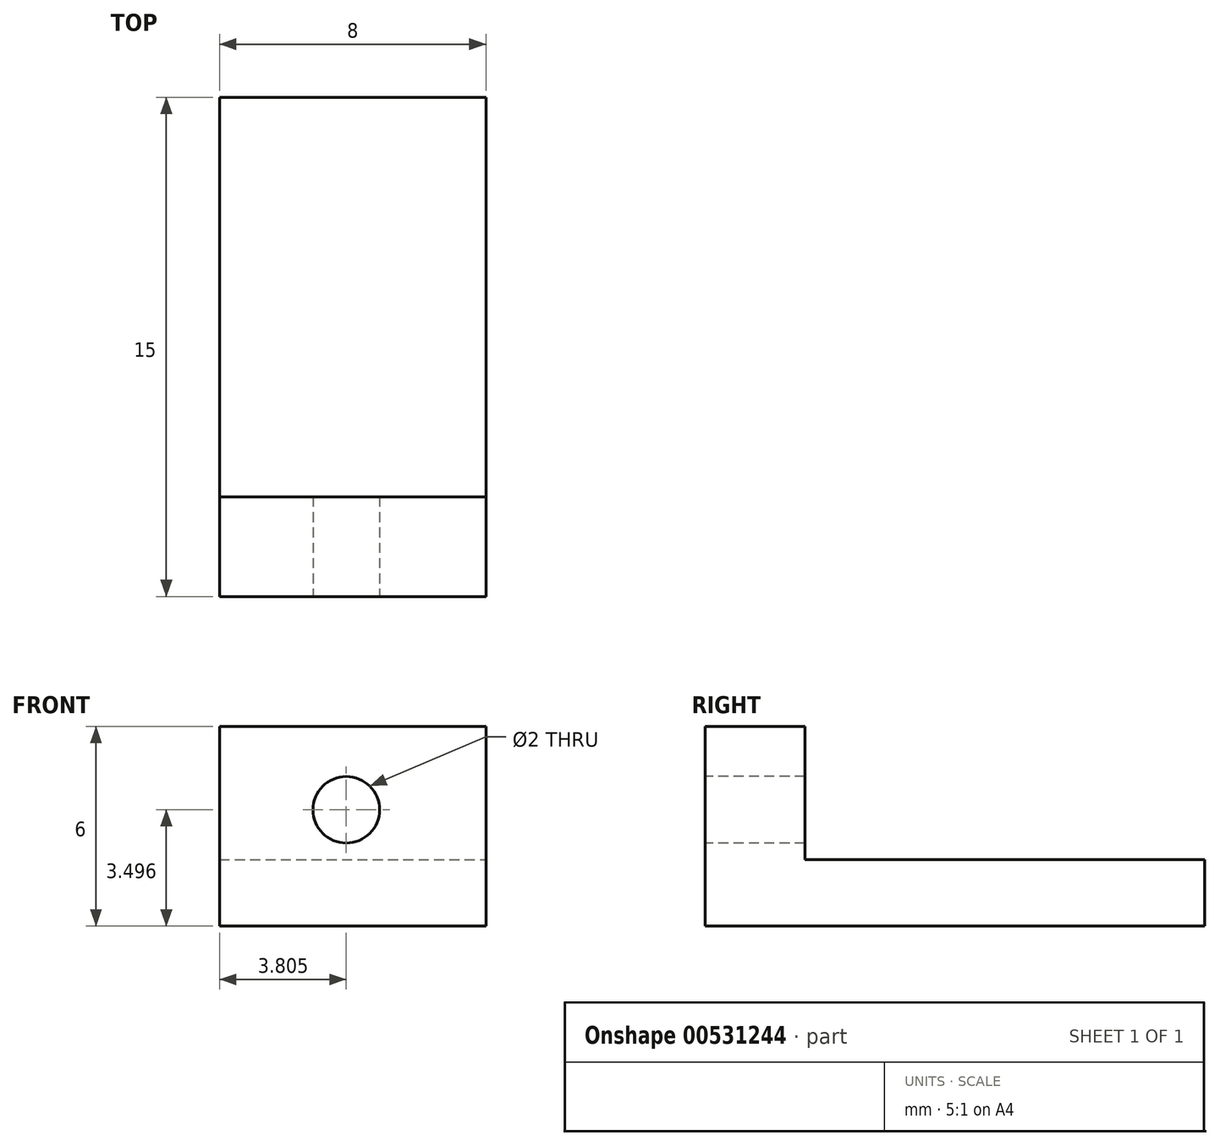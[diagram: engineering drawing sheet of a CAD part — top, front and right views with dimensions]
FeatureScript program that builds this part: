
annotation { "Feature Type Name" : "Feature", "Feature Type Description" : "" }
export const myFeature = defineFeature(function(context is Context, id is Id, definition is map)
    precondition{}
    {
        {
            var Q0;
            Q0=qCreatedBy(makeId("Right.planeOp"),FACE);
            var sketch = newSketch(context, id + "F0", { "sketchPlane" : qUnion([Q0])});
            skLineSegment(sketch, "E0", {"start": v(-31.71, 19.28) * mm, "end": v(-16.71, 19.28) * mm});
            skLineSegment(sketch, "E1", {"start": v(-16.71, 19.28) * mm, "end": v(-16.71, 17.28) * mm});
            skLineSegment(sketch, "E2", {"start": v(-16.71, 17.28) * mm, "end": v(-31.71, 17.28) * mm});
            skLineSegment(sketch, "E3", {"start": v(-31.71, 17.28) * mm, "end": v(-31.71, 19.28) * mm});
            skLineSegment(sketch, "E4", {"start": v(-31.71, 19.28) * mm, "end": v(-31.71, 23.28) * mm});
            skLineSegment(sketch, "E5", {"start": v(-31.71, 23.28) * mm, "end": v(-28.71, 23.28) * mm});
            skLineSegment(sketch, "E6", {"start": v(-28.71, 23.28) * mm, "end": v(-28.71, 19.28) * mm});
            skSolve(sketch);
        }
        {
            var Q0;
            {var subQ0=sQuery(id+"F0.wireOp",EDGE,"E4");Q0=makeQuery(id+"F0.imprint","IMPRINT",FACE,{"disambiguationData":[TD([[makeQuery(id+"F0.imprint","IMPRINT",EDGE,{"derivedFrom":subQ0}),-1.0]])]});}
            var Q1;
            {var subQ0=sQuery(id+"F0.wireOp",EDGE,"E1");Q1=makeQuery(id+"F0.imprint","IMPRINT",FACE,{"disambiguationData":[TD([[makeQuery(id+"F0.imprint","IMPRINT",EDGE,{"derivedFrom":subQ0}),-1.0]])]});}
            extrude(context, id + "F1", {"entities" : qUnion([Q0, Q1]), "oppositeDirection" : true, "depth" : 8 * mm, "offsetDistance" : 25 * mm});
        }
        {
            var Q0;
            Q0=makeQuery(id+"F1.opExtrude","SWEPT_FACE",FACE,{"disambiguationData":[OSD([sQuery(id+"F0.wireOp",EDGE,"E4")])]});
            var sketch = newSketch(context, id + "F2", { "sketchPlane" : qUnion([Q0])});
            skCircle(sketch, "E7", {"center": v(-4.2, 20.78) * mm, "radius": 1 * mm});
            skSolve(sketch);
        }
        {
            var Q0;
            Q0=makeQuery(id+"F2.imprint","IMPRINT",FACE,{"disambiguationData":[TD([[makeQuery(id+"F2.imprint","IMPRINT",EDGE,{"derivedFrom":sQuery(id+"F2.wireOp",EDGE,"E7")}),1.0]])]});
            extrude(context, id + "F3", {"entities" : qUnion([Q0]), "operationType" : NewBodyOperationType.REMOVE, "oppositeDirection" : true, "depth" : 4 * mm, "offsetDistance" : 25 * mm});
        }
    });
